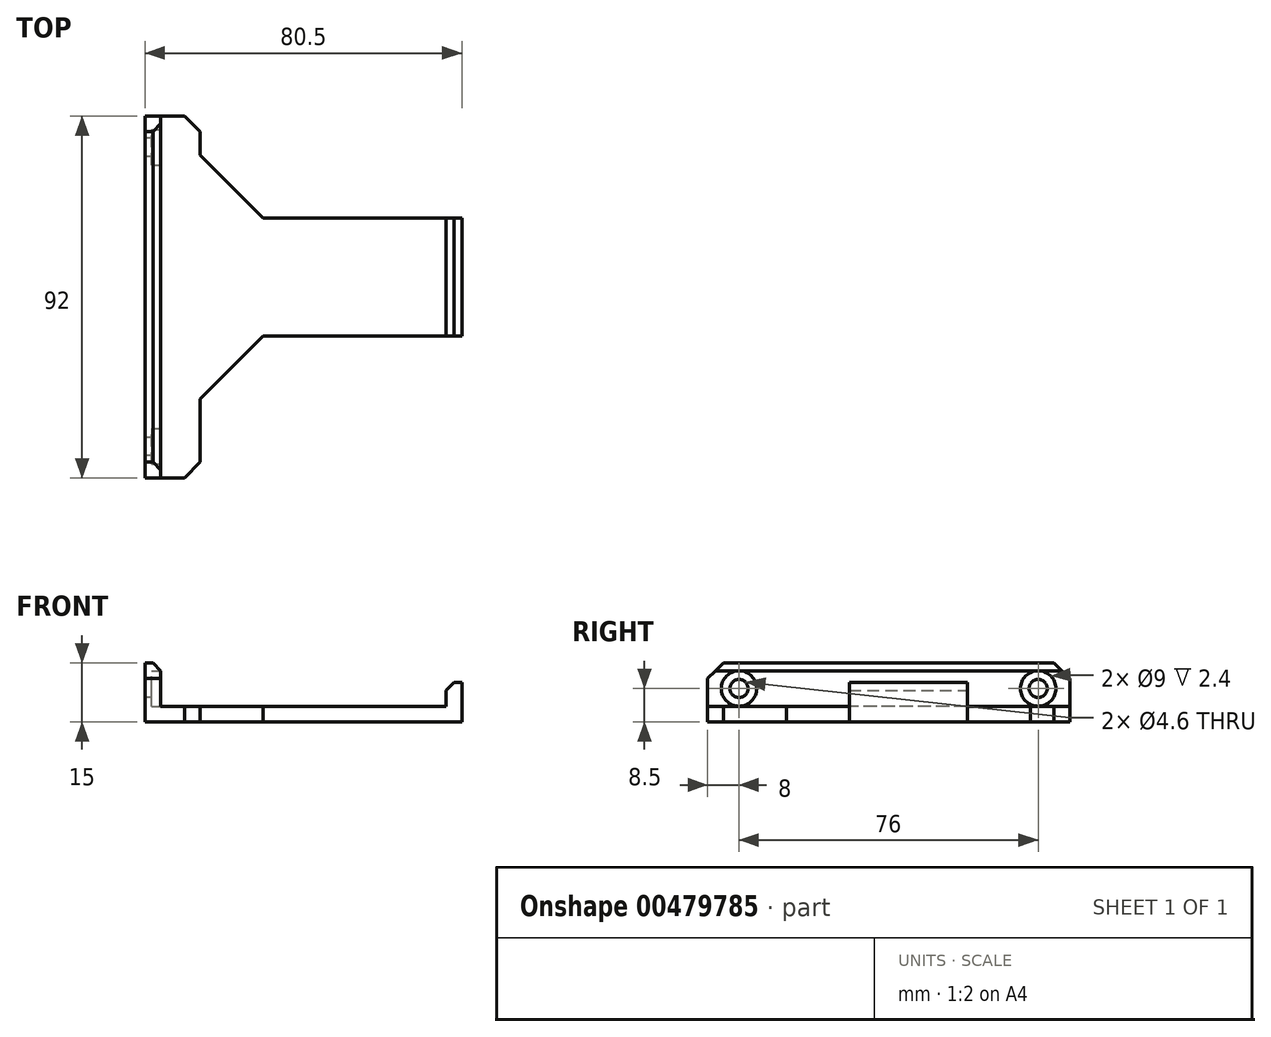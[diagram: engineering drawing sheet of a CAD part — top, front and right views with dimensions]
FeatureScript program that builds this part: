
annotation { "Feature Type Name" : "Feature", "Feature Type Description" : "" }
export const myFeature = defineFeature(function(context is Context, id is Id, definition is map)
    precondition{}
    {
        {
            var Q0;
            Q0=qCreatedBy(makeId("Top.planeOp"),FACE);
            var sketch = newSketch(context, id + "F0", { "sketchPlane" : qUnion([Q0])});
            skLineSegment(sketch, "E0.bottom", {"start": v(72, -75.5) * mm, "end": v(0, -75.5) * mm});
            skLineSegment(sketch, "E0.top", {"start": v(72, 75.5) * mm, "end": v(0, 75.5) * mm});
            skLineSegment(sketch, "E0.left", {"start": v(72, -75.5) * mm, "end": v(72, 75.5) * mm});
            skPoint(sketch, "E1", {"position": v(0, 38) * mm});
            skPoint(sketch, "E2", {"position": v(0, -38) * mm});
            skPoint(sketch, "E3", {"position": v(72, 0) * mm});
            skLineSegment(sketch, "E4", {"start": v(0, 38) * mm, "end": v(0, -38) * mm});
            skLineSegment(sketch, "E5", {"start": v(0, 75.5) * mm, "end": v(0, 38) * mm});
            skLineSegment(sketch, "E6", {"start": v(0, -38) * mm, "end": v(0, -75.5) * mm});
            skPoint(sketch, "E7", {"position": v(0, 0) * mm});
            skSolve(sketch);
        }
        {
            var Q0;
            Q0=qCreatedBy(makeId("Top.planeOp"),FACE);
            var sketch = newSketch(context, id + "F1", { "sketchPlane" : qUnion([Q0])});
            skLineSegment(sketch, "E8", {"start": v(-4, 46) * mm, "end": v(10, 46) * mm});
            skLineSegment(sketch, "E9", {"start": v(10, 46) * mm, "end": v(10, 20) * mm});
            skLineSegment(sketch, "E10", {"start": v(10, 20) * mm, "end": v(76.5, 20) * mm});
            skLineSegment(sketch, "E11", {"start": v(76.5, 20) * mm, "end": v(76.5, -10) * mm});
            skLineSegment(sketch, "E12", {"start": v(76.5, -10) * mm, "end": v(10, -10) * mm});
            skLineSegment(sketch, "E13", {"start": v(10, -10) * mm, "end": v(10, -46) * mm});
            skLineSegment(sketch, "E14", {"start": v(10, -46) * mm, "end": v(-4, -46) * mm});
            skLineSegment(sketch, "E15", {"start": v(-4, -46) * mm, "end": v(-4, 46) * mm});
            skPoint(sketch, "E16", {"position": v(-4, 0) * mm});
            skPoint(sketch, "E17", {"position": v(0, 0) * mm});
            skPoint(sketch, "E18", {"position": v(76.5, 5) * mm});
            skSolve(sketch);
        }
        {
            var Q0;
            Q0 = qSketchRegion(id + "F1", true);
            extrude(context, id + "F2", {"entities" : qUnion([Q0]), "depth" : 4 * mm});
        }
        {
            var Q0;
            Q0=makeQuery(id+"F2.opExtrude","CAP_FACE",FACE,{"disambiguationData":[OSD([sQuery(id+"F1.wireOp",EDGE,"E8"),sQuery(id+"F1.wireOp",EDGE,"E9"),sQuery(id+"F1.wireOp",EDGE,"E10"),sQuery(id+"F1.wireOp",EDGE,"E11"),sQuery(id+"F1.wireOp",EDGE,"E12"),sQuery(id+"F1.wireOp",EDGE,"E13"),sQuery(id+"F1.wireOp",EDGE,"E14"),sQuery(id+"F1.wireOp",EDGE,"E15")])],"isStart":false});
            var sketch = newSketch(context, id + "F3", { "sketchPlane" : qUnion([Q0])});
            skLineSegment(sketch, "E19.bottom", {"start": v(76.5, 20) * mm, "end": v(72.5, 20) * mm});
            skLineSegment(sketch, "E19.top", {"start": v(76.5, -10) * mm, "end": v(72.5, -10) * mm});
            skLineSegment(sketch, "E19.left", {"start": v(76.5, 20) * mm, "end": v(76.5, -10) * mm});
            skLineSegment(sketch, "E19.right", {"start": v(72.5, 20) * mm, "end": v(72.5, -10) * mm});
            skSolve(sketch);
        }
        {
            var Q0;
            Q0 = qSketchRegion(id + "F3", true);
            extrude(context, id + "F4", {"entities" : qUnion([Q0]), "operationType" : NewBodyOperationType.ADD, "depth" : 6 * mm});
        }
        {
            var Q0;
            Q0=makeQuery(id+"F2.opExtrude","SWEPT_EDGE",EDGE,{"disambiguationData":[OSD([sQuery(id+"F1.wireOp",EDGE,"E9"),sQuery(id+"F1.wireOp",EDGE,"E10")])]});
            var Q1;
            Q1=makeQuery(id+"F2.opExtrude","SWEPT_EDGE",EDGE,{"disambiguationData":[OSD([sQuery(id+"F1.wireOp",EDGE,"E12"),sQuery(id+"F1.wireOp",EDGE,"E13")])]});
            chamfer(context, id + "F5", {"entities" : qUnion([Q0, Q1]), "width" : 16 * mm, "tangentPropagation" : true});
        }
        {
            var Q0;
            Q0=makeQuery(id+"F4.opExtrude","CAP_EDGE",EDGE,{"disambiguationData":[OSD([sQuery(id+"F3.wireOp",EDGE,"E19.right")])],"isStart":false});
            chamfer(context, id + "F6", {"entities" : qUnion([Q0]), "width" : 2 * mm, "tangentPropagation" : true});
        }
        {
            var Q0;
            Q0=makeQuery(id+"F2.opExtrude","SWEPT_EDGE",EDGE,{"disambiguationData":[OSD([sQuery(id+"F1.wireOp",EDGE,"E13"),sQuery(id+"F1.wireOp",EDGE,"E14")])]});
            var Q1;
            Q1=makeQuery(id+"F2.opExtrude","SWEPT_EDGE",EDGE,{"disambiguationData":[OSD([sQuery(id+"F1.wireOp",EDGE,"E8"),sQuery(id+"F1.wireOp",EDGE,"E9")])]});
            chamfer(context, id + "F7", {"entities" : qUnion([Q0, Q1]), "width" : 4 * mm, "tangentPropagation" : true});
        }
        {
            var Q0;
            Q0=makeQuery(id+"F2.opExtrude","CAP_FACE",FACE,{"disambiguationData":[OSD([sQuery(id+"F1.wireOp",EDGE,"E8"),sQuery(id+"F1.wireOp",EDGE,"E9"),sQuery(id+"F1.wireOp",EDGE,"E10"),sQuery(id+"F1.wireOp",EDGE,"E11"),sQuery(id+"F1.wireOp",EDGE,"E12"),sQuery(id+"F1.wireOp",EDGE,"E13"),sQuery(id+"F1.wireOp",EDGE,"E14"),sQuery(id+"F1.wireOp",EDGE,"E15")])],"isStart":false});
            var sketch = newSketch(context, id + "F8", { "sketchPlane" : qUnion([Q0])});
            skPoint(sketch, "E20.oppositeSnap0", {"position": v(1, -46) * mm});
            skLineSegment(sketch, "E20.bottom", {"start": v(-4, 46) * mm, "end": v(0, 46) * mm});
            skLineSegment(sketch, "E20.top", {"start": v(-4, -46) * mm, "end": v(0, -46) * mm});
            skLineSegment(sketch, "E20.left", {"start": v(-4, 46) * mm, "end": v(-4, -46) * mm});
            skLineSegment(sketch, "E20.right", {"start": v(0, 46) * mm, "end": v(0, -46) * mm});
            skSolve(sketch);
        }
        {
            var Q0;
            Q0 = qSketchRegion(id + "F8", true);
            extrude(context, id + "F9", {"entities" : qUnion([Q0]), "operationType" : NewBodyOperationType.ADD, "depth" : 11 * mm});
        }
        {
            var Q0;
            Q0=makeQuery(id+"F9.opExtrude","SWEPT_FACE",FACE,{"disambiguationData":[OSD([sQuery(id+"F8.wireOp",EDGE,"E20.right")])]});
            var sketch = newSketch(context, id + "F10", { "sketchPlane" : qUnion([Q0])});
            skCircle(sketch, "E21", {"center": v(-38, 8.5) * mm, "radius": 4.5 * mm});
            skCircle(sketch, "E22", {"center": v(38, 8.5) * mm, "radius": 4.5 * mm});
            skSolve(sketch);
        }
        {
            var Q0;
            Q0 = qSketchRegion(id + "F10", true);
            extrude(context, id + "F11", {"entities" : qUnion([Q0]), "operationType" : NewBodyOperationType.REMOVE, "oppositeDirection" : true, "depth" : 2.4 * mm});
        }
        {
            var Q0;
            Q0=makeQuery(id+"F9.boolean.opBoolean","MERGE",FACE,{"derivedFrom":[makeQuery(id+"F2.opExtrude","SWEPT_FACE",FACE,{"disambiguationData":[OSD([sQuery(id+"F1.wireOp",EDGE,"E15")])]}),makeQuery(id+"F9.opExtrude","SWEPT_FACE",FACE,{"disambiguationData":[OSD([sQuery(id+"F8.wireOp",EDGE,"E20.left")])]})]});
            var sketch = newSketch(context, id + "F12", { "sketchPlane" : qUnion([Q0])});
            skCircle(sketch, "E23", {"center": v(-38, 8.5) * mm, "radius": 2.3 * mm});
            skCircle(sketch, "E24", {"center": v(38, 8.5) * mm, "radius": 2.3 * mm});
            skSolve(sketch);
        }
        {
            var Q0;
            Q0 = qSketchRegion(id + "F12", true);
            var Q1;
            {var subQ0=sQuery(id+"F8.wireOp",EDGE,"E20.right");var subQ1=makeQuery(id+"F9.opExtrude","SWEPT_FACE",FACE,{"disambiguationData":[OSD([subQ0])]});Q1=makeQuery(id+"F11.boolean.opBoolean","SPLIT",FACE,{"disambiguationData":[TD([makeQuery(id+"F2.opExtrude","CAP_FACE",FACE,{"disambiguationData":[OSD([sQuery(id+"F1.wireOp",EDGE,"E8"),sQuery(id+"F1.wireOp",EDGE,"E9"),sQuery(id+"F1.wireOp",EDGE,"E10"),sQuery(id+"F1.wireOp",EDGE,"E11"),sQuery(id+"F1.wireOp",EDGE,"E12"),sQuery(id+"F1.wireOp",EDGE,"E13"),sQuery(id+"F1.wireOp",EDGE,"E14"),sQuery(id+"F1.wireOp",EDGE,"E15")])],"isStart":false}),subQ1,makeQuery(id+"FVomlmd095yn7xX_1.opChamfer","BLEND_FACE",FACE,{"disambiguationData":[OSD([subQ0])]}),makeQuery(id+"F11.opExtrude","SWEPT_FACE",FACE,{"disambiguationData":[OSD([sQuery(id+"F10.wireOp",EDGE,"E21")])]}),makeQuery(id+"F11.opExtrude","SWEPT_FACE",FACE,{"disambiguationData":[OSD([sQuery(id+"F10.wireOp",EDGE,"E22")])]})])],"derivedFrom":subQ1});}
            extrude(context, id + "F13", {"entities" : qUnion([Q0]), "operationType" : NewBodyOperationType.REMOVE, "endBound" : BoundingType.UP_TO_SURFACE, "oppositeDirection" : true, "endBoundEntityFace" : qUnion([Q1]), "depth" : 25 * mm});
        }
        {
            var Q0;
            Q0=makeQuery(id+"F9.opExtrude","CAP_EDGE",EDGE,{"disambiguationData":[OSD([sQuery(id+"F8.wireOp",EDGE,"E20.top")])],"isStart":false});
            var Q1;
            Q1=makeQuery(id+"F9.opExtrude","CAP_EDGE",EDGE,{"disambiguationData":[OSD([sQuery(id+"F8.wireOp",EDGE,"E20.bottom")])],"isStart":false});
            chamfer(context, id + "F14", {"entities" : qUnion([Q0, Q1]), "width" : 4 * mm, "tangentPropagation" : true});
        }
        {
            var Q0;
            Q0=makeQuery(id+"F9.opExtrude","CAP_EDGE",EDGE,{"disambiguationData":[OSD([sQuery(id+"F8.wireOp",EDGE,"E20.right")])],"isStart":false});
            chamfer(context, id + "F15", {"entities" : qUnion([Q0]), "width" : 2 * mm, "tangentPropagation" : true});
        }
    });
